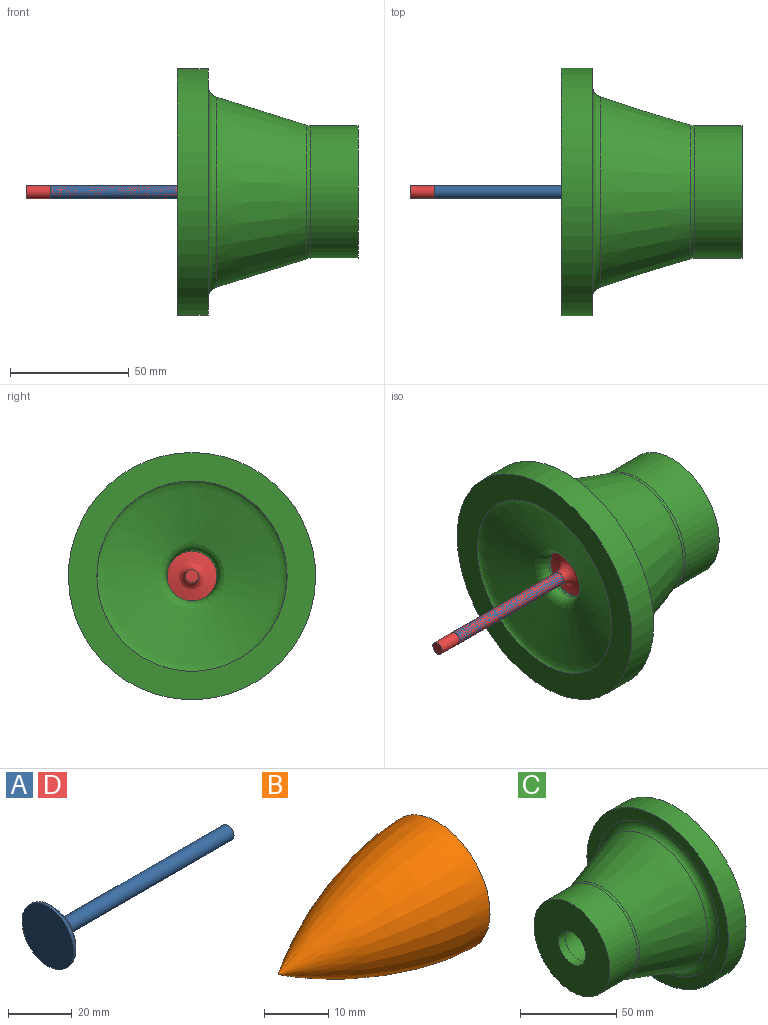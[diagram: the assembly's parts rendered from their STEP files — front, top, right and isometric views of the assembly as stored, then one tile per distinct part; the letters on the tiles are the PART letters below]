
ASSEMBLY  parts=4 mates=4
PART A: 6 faces, bbox 80x23x23 mm
  f0: plane 23x23mm, normal (-1,0,0), area 415.5mm2, adj f5
  f1: plane 5.5x5.5mm, normal (1,0,0), area 23.8mm2, adj f2
  f2: cylinder r=2.75mm len=72.28mm, axis (1,0,0), area 1248.9mm2, adj f1,f3
  f3: revolved ~20.88x20.88mm, area 383.8mm2, adj f2,f4
  f4: cone r=11.5mm half-angle=45deg, axis (-1,0,0), area 103.4mm2, adj f3,f5
  f5: cylinder r=11.5mm len=23mm, axis (1,0,0), area 72.3mm2, adj f0,f4
PART B: 2 faces, bbox 35x23x23 mm
  f0: plane 23x23mm, normal (1,0,0), area 415.5mm2, adj f1
  f1: revolved ~35x23mm, area 1696.1mm2, adj f0
PART C: 13 faces, bbox 76x104.6x104.6 mm
  f0: cone r=10.5mm half-angle=45deg, axis (-1,0,0), area 140.8mm2, adj f1,f10
  f1: cylinder r=10.5mm len=21mm, axis (1,0,0), area 66mm2, adj f0,f2
  f2: revolved ~80x80mm, area 5194.5mm2, adj f1,f3
  f3: plane 104x104mm, normal (1,0,0), area 3468.3mm2, adj f2,f4
  f4: cylinder r=52mm len=104mm, axis (1,0,0), area 4247.4mm2, adj f3,f5
  f5: plane 104x104mm, normal (-1,0,0), area 2204.3mm2, adj f4,f11
  f6: cone r=27.9mm half-angle=17.3deg, axis (1,0,0), area 8503.3mm2, adj f11,f12
  f7: cylinder r=27.9mm len=55.79mm, axis (1,0,0), area 3516.2mm2, adj f8,f12
  f8: plane 55.79x55.79mm, normal (-1,0,0), area 2130.5mm2, adj f7,f9
  f9: cylinder r=10mm len=20mm, axis (1,0,0), area 314.2mm2, adj f8,f10
  f10: revolved ~55.59x33.12mm, area 4850.7mm2, adj f0,f9
  f11: torus R=44.75mm, axis (-1,0,0), area 1672.3mm2, adj f5,f6
  f12: torus R=32.9mm, axis (1,0,0), area 266.1mm2, adj f6,f7
PART D: same geometry as A
PLACE A rot(axis=(0,1,0),180deg) t=(81.64,117.1,-19.8)mm
PLACE B rot(axis=(0,-1,0),180deg) t=(81.64,117.1,-19.8)mm
PLACE C rot(axis=(0,1,0),180deg) t=(130.84,117.1,-19.8)mm
PLACE D rot(axis=(0,1,0),180deg) t=(71.17,117.1,-19.8)mm
MATE cylindrical D.f2 <-> C.f0  axis (-1,0,0) through (63.45,117.1,-19.8)mm
MATE cylindrical A.f2 <-> C.f0  axis (-1,0,0) through (73.91,117.1,-19.8)mm
MATE planar B.f0 <-> A.f2  axis (-1,0,0) through (81.64,117.1,-19.8)mm
MATE cylindrical C.f0 <-> B.f0  axis (-1,0,0) through (120.81,117.1,-19.8)mm
